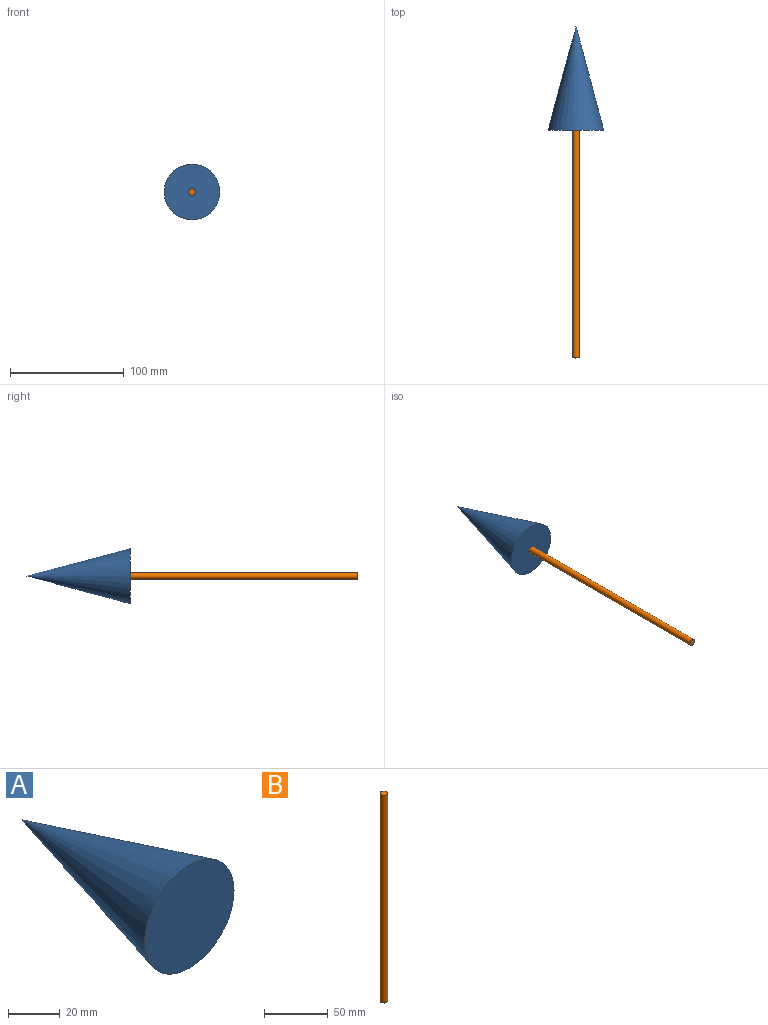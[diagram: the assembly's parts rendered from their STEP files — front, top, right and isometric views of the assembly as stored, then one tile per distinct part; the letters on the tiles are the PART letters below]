
ASSEMBLY  parts=2 mates=1
PART A: 2 faces, bbox 48.8x91.5x48.8 mm
  f0: cone r=0mm half-angle=14.9deg, axis (0,-1,0), area 7257.1mm2, adj f1
  f1: plane 48.81x48.81mm, normal (0,-1,0), area 1871.2mm2, adj f0
PART B: 3 faces, bbox 5.9x5.9x200 mm
  f0: cylinder r=2.96mm len=200mm, axis (0,0,1), area 3722.4mm2, adj f1,f2
  f1: plane 5.92x5.92mm, normal (0,0,1), area 27.6mm2, adj f0
  f2: plane 5.92x5.92mm, normal (0,0,-1), area 27.6mm2, adj f0
PLACE A t=(35.95,30.81,26.38)mm
PLACE B rot(axis=(-1,0,0),90deg) t=(35.95,-207.38,26.38)mm
MATE fastened B.f0 <-> A.f0  axis (0,1,0) through (35.95,-7.38,26.38)mm
